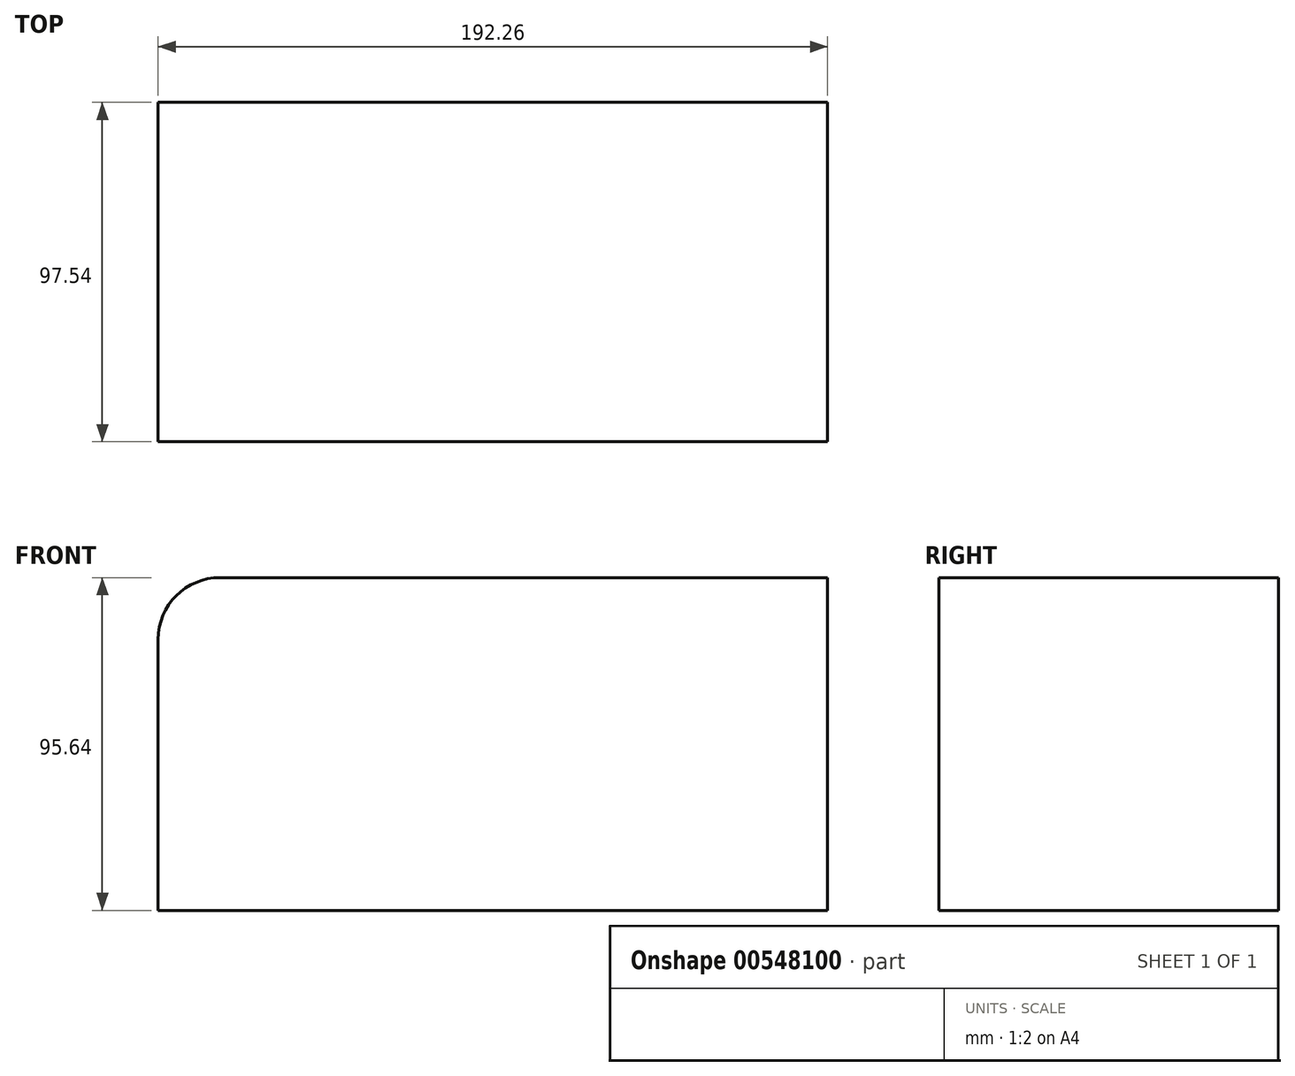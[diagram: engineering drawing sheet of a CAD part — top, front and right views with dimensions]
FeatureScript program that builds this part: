
annotation { "Feature Type Name" : "Feature", "Feature Type Description" : "" }
export const myFeature = defineFeature(function(context is Context, id is Id, definition is map)
    precondition{}
    {
        {
            var Q0;
            Q0=qCreatedBy(makeId("Front.planeOp"),FACE);
            var sketch = newSketch(context, id + "F0", { "sketchPlane" : qUnion([Q0])});
            skLineSegment(sketch, "E0.bottom", {"start": v(-92.4, 66.32) * mm, "end": v(99.85, 66.32) * mm});
            skLineSegment(sketch, "E0.top", {"start": v(-92.4, -29.32) * mm, "end": v(99.85, -29.32) * mm});
            skLineSegment(sketch, "E0.left", {"start": v(-92.4, 66.32) * mm, "end": v(-92.4, -29.32) * mm});
            skLineSegment(sketch, "E0.right", {"start": v(99.85, 66.32) * mm, "end": v(99.85, -29.32) * mm});
            skSolve(sketch);
        }
        {
            var Q0;
            Q0=makeQuery(id+"F0.imprint","IMPRINT",FACE,{"disambiguationData":[TD([[makeQuery(id+"F0.imprint","IMPRINT",EDGE,{"derivedFrom":sQuery(id+"F0.wireOp",EDGE,"E0.bottom")}),-1.0]])]});
            extrude(context, id + "F1", {"entities" : qUnion([Q0]), "endBound" : BoundingType.SYMMETRIC, "depth" : 97.54 * mm, "offsetDistance" : 25.4 * mm});
        }
        {
            var Q0;
            Q0=makeQuery(id+"F1.opExtrude","SWEPT_EDGE",EDGE,{"disambiguationData":[OSD([sQuery(id+"F0.wireOp",EDGE,"E0.bottom"),sQuery(id+"F0.wireOp",EDGE,"E0.left")])]});
            fillet(context, id + "F2", {"entities" : qUnion([Q0]), "radius" : 17.78 * mm, "tangentPropagation" : true, "allowEdgeOverflow" : false});
        }
    });
